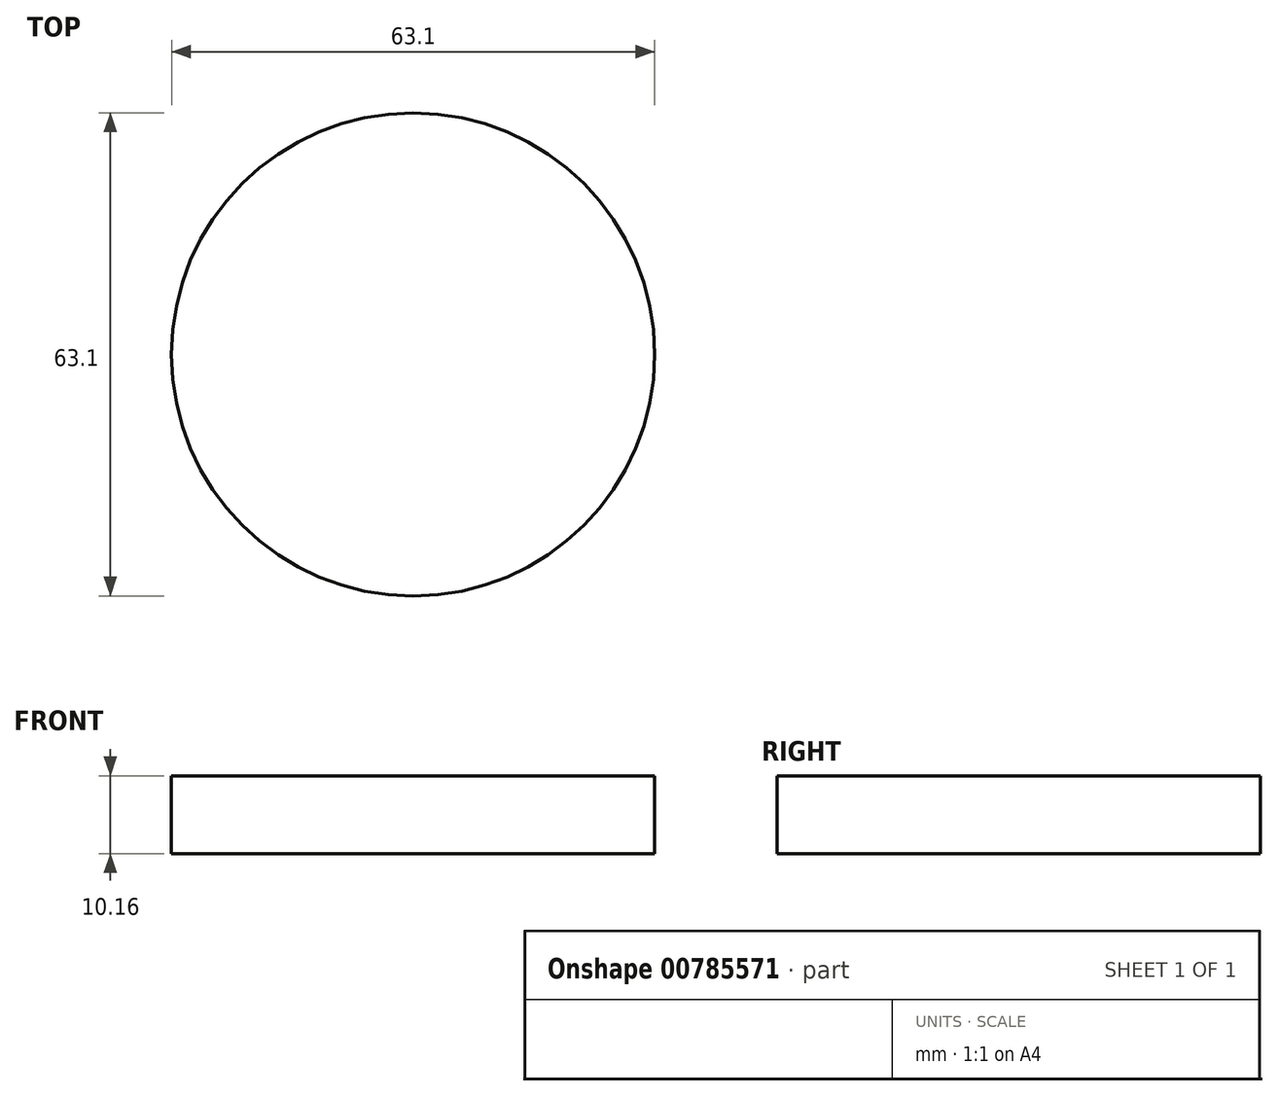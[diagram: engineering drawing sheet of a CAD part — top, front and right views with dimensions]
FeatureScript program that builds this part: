
annotation { "Feature Type Name" : "Feature", "Feature Type Description" : "" }
export const myFeature = defineFeature(function(context is Context, id is Id, definition is map)
    precondition{}
    {
        {
            var Q0;
            Q0=qCreatedBy(makeId("Top.planeOp"),FACE);
            var sketch = newSketch(context, id + "F0", { "sketchPlane" : qUnion([Q0])});
            skCircle(sketch, "E0", {"center": v(0, 0) * mm, "radius": 31.55 * mm});
            skSolve(sketch);
        }
        {
            var Q0;
            Q0=makeQuery(id+"F0.imprint","IMPRINT",FACE,{"disambiguationData":[TD([[makeQuery(id+"F0.imprint","IMPRINT",EDGE,{"derivedFrom":sQuery(id+"F0.wireOp",EDGE,"E0")}),1.0]])]});
            extrude(context, id + "F1", {"entities" : qUnion([Q0]), "depth" : 10.16 * mm, "offsetDistance" : 25.4 * mm});
        }
    });
